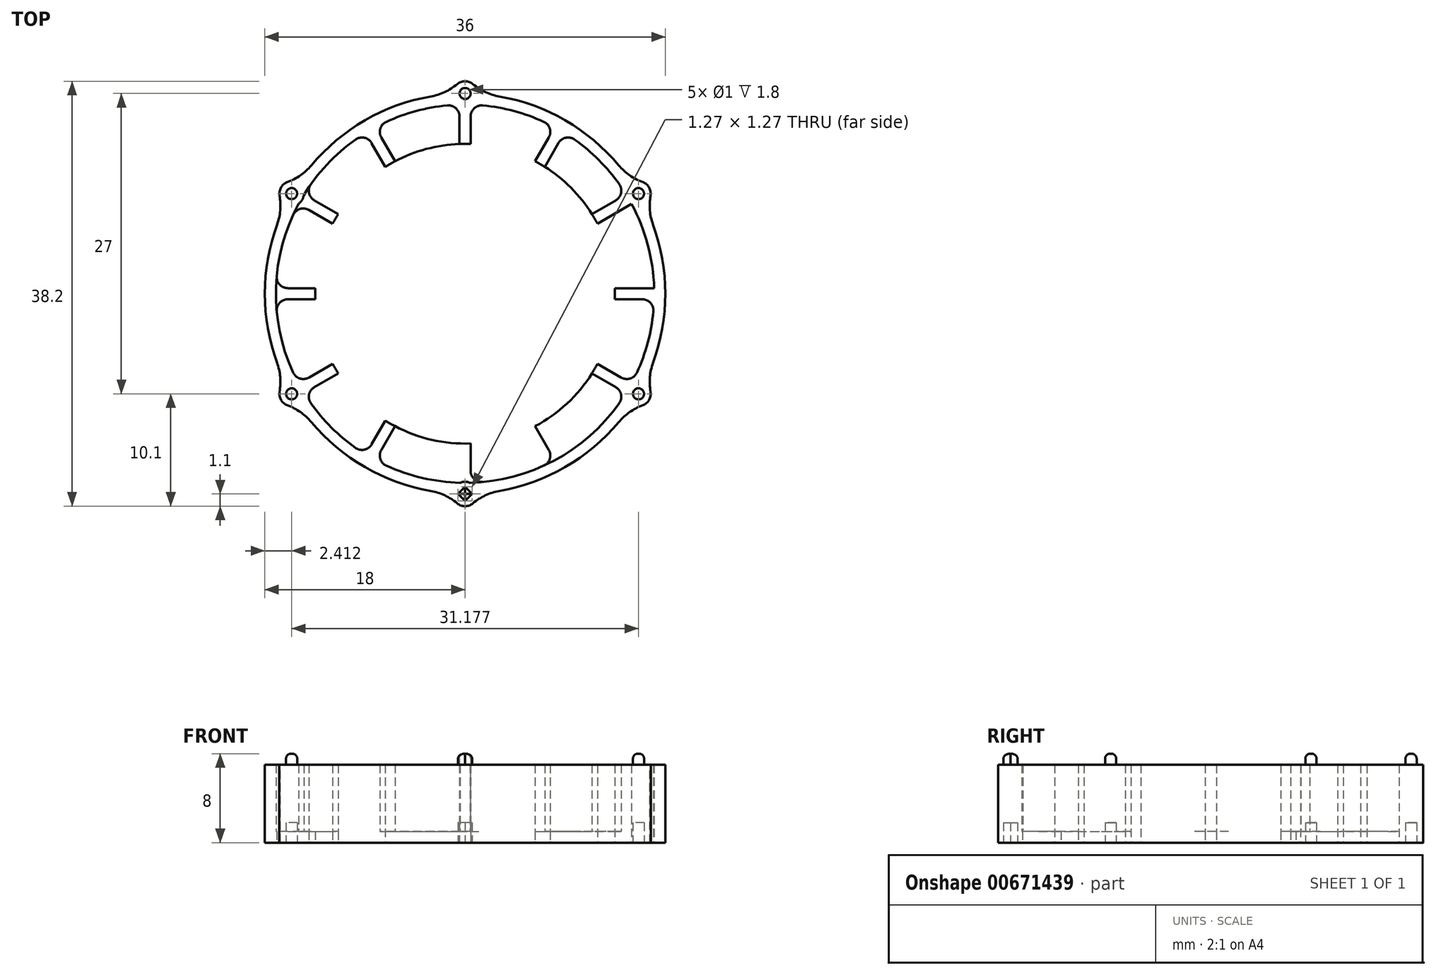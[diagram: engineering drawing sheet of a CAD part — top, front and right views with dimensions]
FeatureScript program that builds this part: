
annotation { "Feature Type Name" : "Feature", "Feature Type Description" : "" }
export const myFeature = defineFeature(function(context is Context, id is Id, definition is map)
    precondition{}
    {
        {
            var Q0;
            Q0=qCreatedBy(makeId("Top.planeOp"),FACE);
            var sketch = newSketch(context, id + "F0", { "sketchPlane" : qUnion([Q0])});
            skCircle(sketch, "E0", {"center": v(0, 0) * mm, "radius": 18 * mm});
            skCircle(sketch, "E1.0", {"center": v(0, 0) * mm, "radius": 17 * mm});
            skLineSegment(sketch, "E2.bottom", {"start": v(8.56, 15.83) * mm, "end": v(9.43, 15.33) * mm});
            skLineSegment(sketch, "E2.top", {"start": v(-9.43, -15.33) * mm, "end": v(-8.56, -15.83) * mm});
            skLineSegment(sketch, "E2.left", {"start": v(8.56, 15.83) * mm, "end": v(-9.43, -15.33) * mm});
            skLineSegment(sketch, "E2.right", {"start": v(9.43, 15.33) * mm, "end": v(-8.56, -15.83) * mm});
            skLineSegment(sketch, "E3.bottom", {"start": v(15.33, 9.43) * mm, "end": v(15.83, 8.56) * mm});
            skLineSegment(sketch, "E3.top", {"start": v(-15.83, -8.56) * mm, "end": v(-15.33, -9.43) * mm});
            skLineSegment(sketch, "E3.left", {"start": v(15.33, 9.43) * mm, "end": v(-15.83, -8.56) * mm});
            skLineSegment(sketch, "E3.right", {"start": v(15.83, 8.56) * mm, "end": v(-15.33, -9.43) * mm});
            skLineSegment(sketch, "E4", {"start": v(-38.35, 0) * mm, "end": v(39.17, 0) * mm, "construction": true});
            skLineSegment(sketch, "E5", {"start": v(0, 42.5) * mm, "end": v(0, -42.47) * mm, "construction": true});
            skLineSegment(sketch, "E6.bottom", {"start": v(-18, 0.5) * mm, "end": v(18, 0.5) * mm});
            skLineSegment(sketch, "E6.top", {"start": v(-18, -0.5) * mm, "end": v(18, -0.5) * mm});
            skLineSegment(sketch, "E6.left", {"start": v(-18, 0.5) * mm, "end": v(-18, -0.5) * mm});
            skLineSegment(sketch, "E6.right", {"start": v(18, 0.5) * mm, "end": v(18, -0.5) * mm});
            skLineSegment(sketch, "E7.bottom", {"start": v(-15.33, 9.43) * mm, "end": v(15.83, -8.56) * mm});
            skLineSegment(sketch, "E7.top", {"start": v(-15.83, 8.56) * mm, "end": v(15.33, -9.43) * mm});
            skLineSegment(sketch, "E7.left", {"start": v(-15.33, 9.43) * mm, "end": v(-15.83, 8.56) * mm});
            skLineSegment(sketch, "E7.right", {"start": v(15.83, -8.56) * mm, "end": v(15.33, -9.43) * mm});
            skLineSegment(sketch, "E8.bottom", {"start": v(-0.5, 18) * mm, "end": v(0.5, 18) * mm});
            skLineSegment(sketch, "E8.top", {"start": v(-0.5, -18) * mm, "end": v(0.5, -18) * mm});
            skLineSegment(sketch, "E8.left", {"start": v(-0.5, 18) * mm, "end": v(-0.5, -18) * mm});
            skLineSegment(sketch, "E8.right", {"start": v(0.5, 18) * mm, "end": v(0.5, -18) * mm});
            skLineSegment(sketch, "E9.bottom", {"start": v(-9.43, 15.33) * mm, "end": v(-8.56, 15.83) * mm});
            skLineSegment(sketch, "E9.top", {"start": v(8.56, -15.83) * mm, "end": v(9.43, -15.33) * mm});
            skLineSegment(sketch, "E9.left", {"start": v(-9.43, 15.33) * mm, "end": v(8.56, -15.83) * mm});
            skLineSegment(sketch, "E9.right", {"start": v(-8.56, 15.83) * mm, "end": v(9.43, -15.33) * mm});
            skCircle(sketch, "E10", {"center": v(0, 0) * mm, "radius": 13.47 * mm});
            skSolve(sketch);
        }
        {
            var Q0;
            Q0=qCreatedBy(makeId("Top.planeOp"),FACE);
            var sketch = newSketch(context, id + "F1", { "sketchPlane" : qUnion([Q0])});
            skCircle(sketch, "E11", {"center": v(0, 0) * mm, "radius": 18 * mm});
            skCircle(sketch, "E12", {"center": v(0, 0) * mm, "radius": 17 * mm});
            skSolve(sketch);
        }
        {
            var Q0;
            Q0=makeQuery(id+"F1.imprint","IMPRINT",FACE,{"disambiguationData":[TD([[makeQuery(id+"F1.imprint","IMPRINT",EDGE,{"derivedFrom":sQuery(id+"F1.wireOp",EDGE,"E11")}),1.0]])]});
            extrude(context, id + "F2", {"entities" : qUnion([Q0]), "depth" : 7 * mm, "offsetDistance" : 25 * mm});
        }
        {
            var Q0;
            {var subQ0=sQuery(id+"F0.wireOp",EDGE,"E2.right");var subQ1=sQuery(id+"F0.wireOp",EDGE,"E1.0");var subQ2=makeQuery(id+"F0.imprint","INTERSECT",VERTEX,{"disambiguationData":[OD(0.0)],"derivedFrom":[subQ1,subQ0]});Q0=makeQuery(id+"F0.imprint","IMPRINT",FACE,{"disambiguationData":[TD([[makeQuery(id+"F0.imprint","IMPRINT",EDGE,{"disambiguationData":[TD([[subQ2,-1.0]])],"derivedFrom":subQ1}),1.0]])]});}
            var Q1;
            {var subQ0=sQuery(id+"F0.wireOp",EDGE,"E6.bottom");var subQ1=sQuery(id+"F0.wireOp",EDGE,"E1.0");var subQ2=makeQuery(id+"F0.imprint","INTERSECT",VERTEX,{"disambiguationData":[OD(0.0)],"derivedFrom":[subQ1,subQ0]});Q1=makeQuery(id+"F0.imprint","IMPRINT",FACE,{"disambiguationData":[TD([[makeQuery(id+"F0.imprint","IMPRINT",EDGE,{"disambiguationData":[TD([[subQ2,1.0]])],"derivedFrom":subQ1}),1.0]])]});}
            var Q2;
            {var subQ0=sQuery(id+"F0.wireOp",EDGE,"E3.left");var subQ1=sQuery(id+"F0.wireOp",EDGE,"E1.0");var subQ2=makeQuery(id+"F0.imprint","INTERSECT",VERTEX,{"disambiguationData":[OD(1.0)],"derivedFrom":[subQ1,subQ0]});Q2=makeQuery(id+"F0.imprint","IMPRINT",FACE,{"disambiguationData":[TD([[makeQuery(id+"F0.imprint","IMPRINT",EDGE,{"disambiguationData":[TD([[subQ2,-1.0]])],"derivedFrom":subQ1}),1.0]])]});}
            var Q3;
            {var subQ0=sQuery(id+"F0.wireOp",EDGE,"E9.right");var subQ1=sQuery(id+"F0.wireOp",EDGE,"E1.0");var subQ2=makeQuery(id+"F0.imprint","INTERSECT",VERTEX,{"disambiguationData":[OD(0.0)],"derivedFrom":[subQ1,subQ0]});Q3=makeQuery(id+"F0.imprint","IMPRINT",FACE,{"disambiguationData":[TD([[makeQuery(id+"F0.imprint","IMPRINT",EDGE,{"disambiguationData":[TD([[subQ2,-1.0]])],"derivedFrom":subQ1}),1.0]])]});}
            var Q4;
            {var subQ0=sQuery(id+"F0.wireOp",EDGE,"E8.right");var subQ1=sQuery(id+"F0.wireOp",EDGE,"E1.0");var subQ2=makeQuery(id+"F0.imprint","INTERSECT",VERTEX,{"disambiguationData":[OD(0.0)],"derivedFrom":[subQ1,subQ0]});Q4=makeQuery(id+"F0.imprint","IMPRINT",FACE,{"disambiguationData":[TD([[makeQuery(id+"F0.imprint","IMPRINT",EDGE,{"disambiguationData":[TD([[subQ2,-1.0]])],"derivedFrom":subQ1}),1.0]])]});}
            var Q5;
            {var subQ0=sQuery(id+"F0.wireOp",EDGE,"E3.right");var subQ1=sQuery(id+"F0.wireOp",EDGE,"E1.0");var subQ2=makeQuery(id+"F0.imprint","INTERSECT",VERTEX,{"disambiguationData":[OD(0.0)],"derivedFrom":[subQ1,subQ0]});Q5=makeQuery(id+"F0.imprint","IMPRINT",FACE,{"disambiguationData":[TD([[makeQuery(id+"F0.imprint","IMPRINT",EDGE,{"disambiguationData":[TD([[subQ2,-1.0]])],"derivedFrom":subQ1}),1.0]])]});}
            var Q6;
            {var subQ0=sQuery(id+"F0.wireOp",EDGE,"E7.top");var subQ1=sQuery(id+"F0.wireOp",EDGE,"E1.0");var subQ2=makeQuery(id+"F0.imprint","INTERSECT",VERTEX,{"disambiguationData":[OD(1.0)],"derivedFrom":[subQ1,subQ0]});Q6=makeQuery(id+"F0.imprint","IMPRINT",FACE,{"disambiguationData":[TD([[makeQuery(id+"F0.imprint","IMPRINT",EDGE,{"disambiguationData":[TD([[subQ2,-1.0]])],"derivedFrom":subQ1}),1.0]])]});}
            var Q7;
            {var subQ0=sQuery(id+"F0.wireOp",EDGE,"E2.left");var subQ1=sQuery(id+"F0.wireOp",EDGE,"E1.0");var subQ2=makeQuery(id+"F0.imprint","INTERSECT",VERTEX,{"disambiguationData":[OD(1.0)],"derivedFrom":[subQ1,subQ0]});Q7=makeQuery(id+"F0.imprint","IMPRINT",FACE,{"disambiguationData":[TD([[makeQuery(id+"F0.imprint","IMPRINT",EDGE,{"disambiguationData":[TD([[subQ2,-1.0]])],"derivedFrom":subQ1}),1.0]])]});}
            extrude(context, id + "F3", {"entities" : qUnion([Q0, Q1, Q2, Q3, Q4, Q5, Q6, Q7]), "operationType" : NewBodyOperationType.ADD, "depth" : 7 * mm, "offsetDistance" : 25 * mm});
        }
        {
            var Q0;
            Q0=makeQuery(id+"F1.imprint","IMPRINT",FACE,{"disambiguationData":[TD([[makeQuery(id+"F1.imprint","IMPRINT",EDGE,{"derivedFrom":sQuery(id+"F1.wireOp",EDGE,"E11")}),1.0]])]});
            var Q1;
            Q1=makeQuery(id+"F1.imprint","IMPRINT",FACE,{"disambiguationData":[TD([[makeQuery(id+"F1.imprint","IMPRINT",EDGE,{"derivedFrom":sQuery(id+"F1.wireOp",EDGE,"E12")}),1.0]])]});
            extrude(context, id + "F4", {"entities" : qUnion([Q0, Q1]), "operationType" : NewBodyOperationType.ADD, "depth" : 1 * mm, "offsetDistance" : 25 * mm});
        }
        {
            var Q0;
            Q0=qCreatedBy(makeId("Top.planeOp"),FACE);
            var sketch = newSketch(context, id + "F5", { "sketchPlane" : qUnion([Q0])});
            skCircle(sketch, "E13", {"center": v(0, 0) * mm, "radius": 18 * mm});
            skLineSegment(sketch, "E14", {"start": v(0, 18) * mm, "end": v(0, -18) * mm, "construction": true});
            skLineSegment(sketch, "E15", {"start": v(15.59, 9) * mm, "end": v(0, 0) * mm, "construction": true});
            skLineSegment(sketch, "E16", {"start": v(9, 15.59) * mm, "end": v(0, 0) * mm, "construction": true});
            skLineSegment(sketch, "E17", {"start": v(0, 0) * mm, "end": v(18, 0) * mm, "construction": true});
            skLineSegment(sketch, "E18", {"start": v(0, 0) * mm, "end": v(15.59, -9) * mm, "construction": true});
            skLineSegment(sketch, "E19", {"start": v(0, 0) * mm, "end": v(9, -15.59) * mm, "construction": true});
            skLineSegment(sketch, "E20", {"start": v(0, 0) * mm, "end": v(-9, 15.59) * mm, "construction": true});
            skLineSegment(sketch, "E21", {"start": v(0, 0) * mm, "end": v(-15.59, 9) * mm, "construction": true});
            skLineSegment(sketch, "E22", {"start": v(0, 0) * mm, "end": v(-18, 0) * mm, "construction": true});
            skLineSegment(sketch, "E23", {"start": v(0, 0) * mm, "end": v(-15.59, -9) * mm, "construction": true});
            skLineSegment(sketch, "E24", {"start": v(0, 0) * mm, "end": v(-9, -15.59) * mm, "construction": true});
            skCircle(sketch, "E25", {"center": v(0, 18) * mm, "radius": 1.1 * mm});
            skCircle(sketch, "E26", {"center": v(15.59, 9) * mm, "radius": 1.1 * mm});
            skCircle(sketch, "E27", {"center": v(15.59, -9) * mm, "radius": 1.1 * mm});
            skCircle(sketch, "E28", {"center": v(0, -18) * mm, "radius": 1.1 * mm});
            skCircle(sketch, "E29", {"center": v(-15.59, -9) * mm, "radius": 1.1 * mm});
            skCircle(sketch, "E30", {"center": v(-15.59, 9) * mm, "radius": 1.1 * mm});
            skCircle(sketch, "E31", {"center": v(-15.59, 9) * mm, "radius": 0.5 * mm});
            skCircle(sketch, "E32", {"center": v(0, 18) * mm, "radius": 0.5 * mm});
            skCircle(sketch, "E33", {"center": v(15.59, 9) * mm, "radius": 0.5 * mm});
            skCircle(sketch, "E34", {"center": v(15.59, -9) * mm, "radius": 0.5 * mm});
            skCircle(sketch, "E35", {"center": v(-15.59, -9) * mm, "radius": 0.5 * mm});
            skLineSegment(sketch, "E36.bottom", {"start": v(0.64, -18) * mm, "end": v(0, -18.64) * mm});
            skLineSegment(sketch, "E36.top", {"start": v(0, -17.36) * mm, "end": v(-0.64, -18) * mm});
            skLineSegment(sketch, "E36.left", {"start": v(0.64, -18) * mm, "end": v(0, -17.36) * mm});
            skLineSegment(sketch, "E36.right", {"start": v(0, -18.64) * mm, "end": v(-0.64, -18) * mm});
            skSolve(sketch);
        }
        {
            var Q0;
            {var subQ0=sQuery(id+"F5.wireOp",EDGE,"E30");var subQ1=sQuery(id+"F5.wireOp",EDGE,"E13");var subQ2=makeQuery(id+"F5.imprint","INTERSECT",VERTEX,{"disambiguationData":[OD(0.0)],"derivedFrom":[subQ1,subQ0]});Q0=makeQuery(id+"F5.imprint","IMPRINT",FACE,{"disambiguationData":[TD([[makeQuery(id+"F5.imprint","IMPRINT",EDGE,{"disambiguationData":[TD([[subQ2,-1.0]])],"derivedFrom":subQ1}),1.0]])]});}
            var Q1;
            {var subQ0=sQuery(id+"F5.wireOp",EDGE,"E30");var subQ1=sQuery(id+"F5.wireOp",EDGE,"E13");var subQ2=makeQuery(id+"F5.imprint","INTERSECT",VERTEX,{"disambiguationData":[OD(0.0)],"derivedFrom":[subQ1,subQ0]});Q1=makeQuery(id+"F5.imprint","IMPRINT",FACE,{"disambiguationData":[TD([[makeQuery(id+"F5.imprint","IMPRINT",EDGE,{"disambiguationData":[TD([[subQ2,-1.0]])],"derivedFrom":subQ1}),-1.0]])]});}
            var Q2;
            {var subQ0=sQuery(id+"F5.wireOp",EDGE,"E25");var subQ1=sQuery(id+"F5.wireOp",EDGE,"E13");var subQ2=makeQuery(id+"F5.imprint","INTERSECT",VERTEX,{"disambiguationData":[OD(0.0)],"derivedFrom":[subQ1,subQ0]});Q2=makeQuery(id+"F5.imprint","IMPRINT",FACE,{"disambiguationData":[TD([[makeQuery(id+"F5.imprint","IMPRINT",EDGE,{"disambiguationData":[TD([[subQ2,-1.0]])],"derivedFrom":subQ1}),1.0]])]});}
            var Q3;
            {var subQ0=sQuery(id+"F5.wireOp",EDGE,"E25");var subQ1=sQuery(id+"F5.wireOp",EDGE,"E13");var subQ2=makeQuery(id+"F5.imprint","INTERSECT",VERTEX,{"disambiguationData":[OD(0.0)],"derivedFrom":[subQ1,subQ0]});Q3=makeQuery(id+"F5.imprint","IMPRINT",FACE,{"disambiguationData":[TD([[makeQuery(id+"F5.imprint","IMPRINT",EDGE,{"disambiguationData":[TD([[subQ2,-1.0]])],"derivedFrom":subQ1}),-1.0]])]});}
            var Q4;
            {var subQ0=sQuery(id+"F5.wireOp",EDGE,"E26");var subQ1=sQuery(id+"F5.wireOp",EDGE,"E13");var subQ2=makeQuery(id+"F5.imprint","INTERSECT",VERTEX,{"disambiguationData":[OD(0.0)],"derivedFrom":[subQ1,subQ0]});Q4=makeQuery(id+"F5.imprint","IMPRINT",FACE,{"disambiguationData":[TD([[makeQuery(id+"F5.imprint","IMPRINT",EDGE,{"disambiguationData":[TD([[subQ2,-1.0]])],"derivedFrom":subQ1}),-1.0]])]});}
            var Q5;
            {var subQ0=sQuery(id+"F5.wireOp",EDGE,"E26");var subQ1=sQuery(id+"F5.wireOp",EDGE,"E13");var subQ2=makeQuery(id+"F5.imprint","INTERSECT",VERTEX,{"disambiguationData":[OD(0.0)],"derivedFrom":[subQ1,subQ0]});Q5=makeQuery(id+"F5.imprint","IMPRINT",FACE,{"disambiguationData":[TD([[makeQuery(id+"F5.imprint","IMPRINT",EDGE,{"disambiguationData":[TD([[subQ2,-1.0]])],"derivedFrom":subQ1}),1.0]])]});}
            var Q6;
            {var subQ0=sQuery(id+"F5.wireOp",EDGE,"E29");var subQ1=sQuery(id+"F5.wireOp",EDGE,"E13");var subQ2=makeQuery(id+"F5.imprint","INTERSECT",VERTEX,{"disambiguationData":[OD(0.0)],"derivedFrom":[subQ1,subQ0]});Q6=makeQuery(id+"F5.imprint","IMPRINT",FACE,{"disambiguationData":[TD([[makeQuery(id+"F5.imprint","IMPRINT",EDGE,{"disambiguationData":[TD([[subQ2,-1.0]])],"derivedFrom":subQ1}),1.0]])]});}
            var Q7;
            {var subQ0=sQuery(id+"F5.wireOp",EDGE,"E29");var subQ1=sQuery(id+"F5.wireOp",EDGE,"E13");var subQ2=makeQuery(id+"F5.imprint","INTERSECT",VERTEX,{"disambiguationData":[OD(0.0)],"derivedFrom":[subQ1,subQ0]});Q7=makeQuery(id+"F5.imprint","IMPRINT",FACE,{"disambiguationData":[TD([[makeQuery(id+"F5.imprint","IMPRINT",EDGE,{"disambiguationData":[TD([[subQ2,-1.0]])],"derivedFrom":subQ1}),-1.0]])]});}
            var Q8;
            {var subQ3=sQuery(id+"F5.wireOp",EDGE,"E13");var subQ5=sQuery(id+"F5.wireOp",EDGE,"E28");var subQ6=makeQuery(id+"F5.imprint","INTERSECT",VERTEX,{"disambiguationData":[OD(0.0)],"derivedFrom":[subQ3,subQ5]});Q8=makeQuery(id+"F5.imprint","IMPRINT",FACE,{"disambiguationData":[TD([[makeQuery(id+"F5.imprint","IMPRINT",EDGE,{"disambiguationData":[TD([[subQ6,-1.0]])],"derivedFrom":subQ3}),1.0]])]});}
            var Q9;
            {var subQ6=sQuery(id+"F5.wireOp",EDGE,"E36.bottom");Q9=makeQuery(id+"F5.imprint","IMPRINT",FACE,{"disambiguationData":[TD([[makeQuery(id+"F5.imprint","IMPRINT",EDGE,{"derivedFrom":subQ6}),1.0]])]});}
            var Q10;
            {var subQ0=sQuery(id+"F5.wireOp",EDGE,"E27");var subQ1=sQuery(id+"F5.wireOp",EDGE,"E13");var subQ2=makeQuery(id+"F5.imprint","INTERSECT",VERTEX,{"disambiguationData":[OD(0.0)],"derivedFrom":[subQ1,subQ0]});Q10=makeQuery(id+"F5.imprint","IMPRINT",FACE,{"disambiguationData":[TD([[makeQuery(id+"F5.imprint","IMPRINT",EDGE,{"disambiguationData":[TD([[subQ2,-1.0]])],"derivedFrom":subQ1}),-1.0]])]});}
            var Q11;
            {var subQ0=sQuery(id+"F5.wireOp",EDGE,"E27");var subQ1=sQuery(id+"F5.wireOp",EDGE,"E13");var subQ2=makeQuery(id+"F5.imprint","INTERSECT",VERTEX,{"disambiguationData":[OD(0.0)],"derivedFrom":[subQ1,subQ0]});Q11=makeQuery(id+"F5.imprint","IMPRINT",FACE,{"disambiguationData":[TD([[makeQuery(id+"F5.imprint","IMPRINT",EDGE,{"disambiguationData":[TD([[subQ2,-1.0]])],"derivedFrom":subQ1}),1.0]])]});}
            var Q12;
            {var subQ0=sQuery(id+"F5.wireOp",EDGE,"E31");var subQ1=sQuery(id+"F5.wireOp",EDGE,"E13");var subQ2=makeQuery(id+"F5.imprint","INTERSECT",VERTEX,{"disambiguationData":[OD(0.0)],"derivedFrom":[subQ1,subQ0]});Q12=makeQuery(id+"F5.imprint","IMPRINT",FACE,{"disambiguationData":[TD([[makeQuery(id+"F5.imprint","IMPRINT",EDGE,{"disambiguationData":[TD([[subQ2,-1.0]])],"derivedFrom":subQ1}),1.0]])]});}
            var Q13;
            {var subQ0=sQuery(id+"F5.wireOp",EDGE,"E31");var subQ1=sQuery(id+"F5.wireOp",EDGE,"E13");var subQ2=makeQuery(id+"F5.imprint","INTERSECT",VERTEX,{"disambiguationData":[OD(0.0)],"derivedFrom":[subQ1,subQ0]});Q13=makeQuery(id+"F5.imprint","IMPRINT",FACE,{"disambiguationData":[TD([[makeQuery(id+"F5.imprint","IMPRINT",EDGE,{"disambiguationData":[TD([[subQ2,-1.0]])],"derivedFrom":subQ1}),-1.0]])]});}
            var Q14;
            {var subQ0=sQuery(id+"F5.wireOp",EDGE,"E32");var subQ1=sQuery(id+"F5.wireOp",EDGE,"E13");var subQ2=makeQuery(id+"F5.imprint","INTERSECT",VERTEX,{"disambiguationData":[OD(0.0)],"derivedFrom":[subQ1,subQ0]});Q14=makeQuery(id+"F5.imprint","IMPRINT",FACE,{"disambiguationData":[TD([[makeQuery(id+"F5.imprint","IMPRINT",EDGE,{"disambiguationData":[TD([[subQ2,-1.0]])],"derivedFrom":subQ1}),-1.0]])]});}
            var Q15;
            {var subQ0=sQuery(id+"F5.wireOp",EDGE,"E32");var subQ1=sQuery(id+"F5.wireOp",EDGE,"E13");var subQ2=makeQuery(id+"F5.imprint","INTERSECT",VERTEX,{"disambiguationData":[OD(0.0)],"derivedFrom":[subQ1,subQ0]});Q15=makeQuery(id+"F5.imprint","IMPRINT",FACE,{"disambiguationData":[TD([[makeQuery(id+"F5.imprint","IMPRINT",EDGE,{"disambiguationData":[TD([[subQ2,-1.0]])],"derivedFrom":subQ1}),1.0]])]});}
            var Q16;
            {var subQ0=sQuery(id+"F5.wireOp",EDGE,"E33");var subQ1=sQuery(id+"F5.wireOp",EDGE,"E13");var subQ2=makeQuery(id+"F5.imprint","INTERSECT",VERTEX,{"disambiguationData":[OD(0.0)],"derivedFrom":[subQ1,subQ0]});Q16=makeQuery(id+"F5.imprint","IMPRINT",FACE,{"disambiguationData":[TD([[makeQuery(id+"F5.imprint","IMPRINT",EDGE,{"disambiguationData":[TD([[subQ2,-1.0]])],"derivedFrom":subQ1}),-1.0]])]});}
            var Q17;
            {var subQ0=sQuery(id+"F5.wireOp",EDGE,"E33");var subQ1=sQuery(id+"F5.wireOp",EDGE,"E13");var subQ2=makeQuery(id+"F5.imprint","INTERSECT",VERTEX,{"disambiguationData":[OD(0.0)],"derivedFrom":[subQ1,subQ0]});Q17=makeQuery(id+"F5.imprint","IMPRINT",FACE,{"disambiguationData":[TD([[makeQuery(id+"F5.imprint","IMPRINT",EDGE,{"disambiguationData":[TD([[subQ2,-1.0]])],"derivedFrom":subQ1}),1.0]])]});}
            var Q18;
            {var subQ0=sQuery(id+"F5.wireOp",EDGE,"E34");var subQ1=sQuery(id+"F5.wireOp",EDGE,"E13");var subQ2=makeQuery(id+"F5.imprint","INTERSECT",VERTEX,{"disambiguationData":[OD(0.0)],"derivedFrom":[subQ1,subQ0]});Q18=makeQuery(id+"F5.imprint","IMPRINT",FACE,{"disambiguationData":[TD([[makeQuery(id+"F5.imprint","IMPRINT",EDGE,{"disambiguationData":[TD([[subQ2,-1.0]])],"derivedFrom":subQ1}),-1.0]])]});}
            var Q19;
            {var subQ0=sQuery(id+"F5.wireOp",EDGE,"E34");var subQ1=sQuery(id+"F5.wireOp",EDGE,"E13");var subQ2=makeQuery(id+"F5.imprint","INTERSECT",VERTEX,{"disambiguationData":[OD(0.0)],"derivedFrom":[subQ1,subQ0]});Q19=makeQuery(id+"F5.imprint","IMPRINT",FACE,{"disambiguationData":[TD([[makeQuery(id+"F5.imprint","IMPRINT",EDGE,{"disambiguationData":[TD([[subQ2,-1.0]])],"derivedFrom":subQ1}),1.0]])]});}
            var Q20;
            {var subQ1=sQuery(id+"F5.wireOp",EDGE,"E36.bottom");Q20=makeQuery(id+"F5.imprint","IMPRINT",FACE,{"disambiguationData":[TD([[makeQuery(id+"F5.imprint","IMPRINT",EDGE,{"derivedFrom":subQ1}),-1.0]])]});}
            var Q21;
            {var subQ0=sQuery(id+"F5.wireOp",EDGE,"E35");var subQ1=sQuery(id+"F5.wireOp",EDGE,"E13");var subQ2=makeQuery(id+"F5.imprint","INTERSECT",VERTEX,{"disambiguationData":[OD(0.0)],"derivedFrom":[subQ1,subQ0]});Q21=makeQuery(id+"F5.imprint","IMPRINT",FACE,{"disambiguationData":[TD([[makeQuery(id+"F5.imprint","IMPRINT",EDGE,{"disambiguationData":[TD([[subQ2,-1.0]])],"derivedFrom":subQ1}),-1.0]])]});}
            var Q22;
            {var subQ0=sQuery(id+"F5.wireOp",EDGE,"E35");var subQ1=sQuery(id+"F5.wireOp",EDGE,"E13");var subQ2=makeQuery(id+"F5.imprint","INTERSECT",VERTEX,{"disambiguationData":[OD(0.0)],"derivedFrom":[subQ1,subQ0]});Q22=makeQuery(id+"F5.imprint","IMPRINT",FACE,{"disambiguationData":[TD([[makeQuery(id+"F5.imprint","IMPRINT",EDGE,{"disambiguationData":[TD([[subQ2,-1.0]])],"derivedFrom":subQ1}),1.0]])]});}
            var Q23;
            {var subQ0=sQuery(id+"F5.wireOp",EDGE,"E36.top");var subQ1=sQuery(id+"F5.wireOp",EDGE,"E13");var subQ2=makeQuery(id+"F5.imprint","INTERSECT",VERTEX,{"derivedFrom":[subQ1,subQ0]});Q23=makeQuery(id+"F5.imprint","IMPRINT",FACE,{"disambiguationData":[TD([[makeQuery(id+"F5.imprint","IMPRINT",EDGE,{"disambiguationData":[TD([[subQ2,-1.0]])],"derivedFrom":subQ1}),1.0]])]});}
            extrude(context, id + "F6", {"entities" : qUnion([Q0, Q1, Q2, Q3, Q4, Q5, Q6, Q7, Q8, Q9, Q10, Q11, Q12, Q13, Q14, Q15, Q16, Q17, Q18, Q19, Q20, Q21, Q22, Q23]), "operationType" : NewBodyOperationType.ADD, "depth" : 7 * mm, "offsetDistance" : 25 * mm});
        }
        {
            var Q0;
            {var subQ0=sQuery(id+"F0.wireOp",EDGE,"E8.right");var subQ1=sQuery(id+"F0.wireOp",EDGE,"E1.0");Q0=makeQuery(id+"F3.opExtrude","SWEPT_EDGE",EDGE,{"disambiguationData":[OSD([subQ1,subQ0]),TDD([makeQuery(id+"F0.imprint","INTERSECT",VERTEX,{"disambiguationData":[OD(1.0)],"derivedFrom":[subQ1,subQ0]})])]});}
            var Q1;
            {var subQ0=sQuery(id+"F0.wireOp",EDGE,"E2.left");var subQ1=sQuery(id+"F0.wireOp",EDGE,"E1.0");Q1=makeQuery(id+"F3.opExtrude","SWEPT_EDGE",EDGE,{"disambiguationData":[OSD([subQ1,subQ0]),TDD([makeQuery(id+"F0.imprint","INTERSECT",VERTEX,{"disambiguationData":[OD(1.0)],"derivedFrom":[subQ1,subQ0]})])]});}
            var Q2;
            {var subQ0=sQuery(id+"F0.wireOp",EDGE,"E3.left");var subQ1=sQuery(id+"F0.wireOp",EDGE,"E1.0");Q2=makeQuery(id+"F3.opExtrude","SWEPT_EDGE",EDGE,{"disambiguationData":[OSD([subQ1,subQ0]),TDD([makeQuery(id+"F0.imprint","INTERSECT",VERTEX,{"disambiguationData":[OD(1.0)],"derivedFrom":[subQ1,subQ0]})])]});}
            var Q3;
            {var subQ0=sQuery(id+"F0.wireOp",EDGE,"E6.bottom");var subQ1=sQuery(id+"F0.wireOp",EDGE,"E1.0");Q3=makeQuery(id+"F3.opExtrude","SWEPT_EDGE",EDGE,{"disambiguationData":[OSD([subQ1,subQ0]),TDD([makeQuery(id+"F0.imprint","INTERSECT",VERTEX,{"disambiguationData":[OD(1.0)],"derivedFrom":[subQ1,subQ0]})])]});}
            var Q4;
            {var subQ0=sQuery(id+"F0.wireOp",EDGE,"E9.right");var subQ1=sQuery(id+"F0.wireOp",EDGE,"E1.0");Q4=makeQuery(id+"F3.opExtrude","SWEPT_EDGE",EDGE,{"disambiguationData":[OSD([subQ1,subQ0]),TDD([makeQuery(id+"F0.imprint","INTERSECT",VERTEX,{"disambiguationData":[OD(1.0)],"derivedFrom":[subQ1,subQ0]})])]});}
            var Q5;
            {var subQ0=sQuery(id+"F0.wireOp",EDGE,"E7.bottom");var subQ1=sQuery(id+"F0.wireOp",EDGE,"E1.0");Q5=makeQuery(id+"F3.opExtrude","SWEPT_EDGE",EDGE,{"disambiguationData":[OSD([subQ1,subQ0]),TDD([makeQuery(id+"F0.imprint","INTERSECT",VERTEX,{"disambiguationData":[OD(1.0)],"derivedFrom":[subQ1,subQ0]})])]});}
            var Q6;
            {var subQ0=sQuery(id+"F0.wireOp",EDGE,"E8.left");var subQ1=sQuery(id+"F0.wireOp",EDGE,"E1.0");Q6=makeQuery(id+"F3.opExtrude","SWEPT_EDGE",EDGE,{"disambiguationData":[OSD([subQ1,subQ0]),TDD([makeQuery(id+"F0.imprint","INTERSECT",VERTEX,{"disambiguationData":[OD(0.0)],"derivedFrom":[subQ1,subQ0]})])]});}
            var Q7;
            {var subQ0=sQuery(id+"F0.wireOp",EDGE,"E2.left");var subQ1=sQuery(id+"F0.wireOp",EDGE,"E1.0");Q7=makeQuery(id+"F3.opExtrude","SWEPT_EDGE",EDGE,{"disambiguationData":[OSD([subQ1,subQ0]),TDD([makeQuery(id+"F0.imprint","INTERSECT",VERTEX,{"disambiguationData":[OD(0.0)],"derivedFrom":[subQ1,subQ0]})])]});}
            var Q8;
            {var subQ0=sQuery(id+"F0.wireOp",EDGE,"E3.left");var subQ1=sQuery(id+"F0.wireOp",EDGE,"E1.0");Q8=makeQuery(id+"F3.opExtrude","SWEPT_EDGE",EDGE,{"disambiguationData":[OSD([subQ1,subQ0]),TDD([makeQuery(id+"F0.imprint","INTERSECT",VERTEX,{"disambiguationData":[OD(0.0)],"derivedFrom":[subQ1,subQ0]})])]});}
            var Q9;
            {var subQ0=sQuery(id+"F0.wireOp",EDGE,"E6.top");var subQ1=sQuery(id+"F0.wireOp",EDGE,"E1.0");Q9=makeQuery(id+"F3.opExtrude","SWEPT_EDGE",EDGE,{"disambiguationData":[OSD([subQ1,subQ0]),TDD([makeQuery(id+"F0.imprint","INTERSECT",VERTEX,{"disambiguationData":[OD(1.0)],"derivedFrom":[subQ1,subQ0]})])]});}
            var Q10;
            {var subQ0=sQuery(id+"F0.wireOp",EDGE,"E7.top");var subQ1=sQuery(id+"F0.wireOp",EDGE,"E1.0");Q10=makeQuery(id+"F3.opExtrude","SWEPT_EDGE",EDGE,{"disambiguationData":[OSD([subQ1,subQ0]),TDD([makeQuery(id+"F0.imprint","INTERSECT",VERTEX,{"disambiguationData":[OD(0.0)],"derivedFrom":[subQ1,subQ0]})])]});}
            var Q11;
            {var subQ0=sQuery(id+"F0.wireOp",EDGE,"E6.top");var subQ1=sQuery(id+"F0.wireOp",EDGE,"E1.0");Q11=makeQuery(id+"F3.opExtrude","SWEPT_EDGE",EDGE,{"disambiguationData":[OSD([subQ1,subQ0]),TDD([makeQuery(id+"F0.imprint","INTERSECT",VERTEX,{"disambiguationData":[OD(0.0)],"derivedFrom":[subQ1,subQ0]})])]});}
            var Q12;
            {var subQ0=sQuery(id+"F0.wireOp",EDGE,"E9.left");var subQ1=sQuery(id+"F0.wireOp",EDGE,"E1.0");Q12=makeQuery(id+"F3.opExtrude","SWEPT_EDGE",EDGE,{"disambiguationData":[OSD([subQ1,subQ0]),TDD([makeQuery(id+"F0.imprint","INTERSECT",VERTEX,{"disambiguationData":[OD(0.0)],"derivedFrom":[subQ1,subQ0]})])]});}
            var Q13;
            {var subQ0=sQuery(id+"F0.wireOp",EDGE,"E8.right");var subQ1=sQuery(id+"F0.wireOp",EDGE,"E1.0");Q13=makeQuery(id+"F3.opExtrude","SWEPT_EDGE",EDGE,{"disambiguationData":[OSD([subQ1,subQ0]),TDD([makeQuery(id+"F0.imprint","INTERSECT",VERTEX,{"disambiguationData":[OD(0.0)],"derivedFrom":[subQ1,subQ0]})])]});}
            var Q14;
            {var subQ0=sQuery(id+"F0.wireOp",EDGE,"E7.bottom");var subQ1=sQuery(id+"F0.wireOp",EDGE,"E1.0");Q14=makeQuery(id+"F3.opExtrude","SWEPT_EDGE",EDGE,{"disambiguationData":[OSD([subQ1,subQ0]),TDD([makeQuery(id+"F0.imprint","INTERSECT",VERTEX,{"disambiguationData":[OD(0.0)],"derivedFrom":[subQ1,subQ0]})])]});}
            var Q15;
            {var subQ0=sQuery(id+"F0.wireOp",EDGE,"E9.right");var subQ1=sQuery(id+"F0.wireOp",EDGE,"E1.0");Q15=makeQuery(id+"F3.opExtrude","SWEPT_EDGE",EDGE,{"disambiguationData":[OSD([subQ1,subQ0]),TDD([makeQuery(id+"F0.imprint","INTERSECT",VERTEX,{"disambiguationData":[OD(0.0)],"derivedFrom":[subQ1,subQ0]})])]});}
            var Q16;
            {var subQ0=sQuery(id+"F0.wireOp",EDGE,"E3.right");var subQ1=sQuery(id+"F0.wireOp",EDGE,"E1.0");Q16=makeQuery(id+"F3.opExtrude","SWEPT_EDGE",EDGE,{"disambiguationData":[OSD([subQ1,subQ0]),TDD([makeQuery(id+"F0.imprint","INTERSECT",VERTEX,{"disambiguationData":[OD(1.0)],"derivedFrom":[subQ1,subQ0]})])]});}
            var Q17;
            {var subQ0=sQuery(id+"F0.wireOp",EDGE,"E2.right");var subQ1=sQuery(id+"F0.wireOp",EDGE,"E1.0");Q17=makeQuery(id+"F3.opExtrude","SWEPT_EDGE",EDGE,{"disambiguationData":[OSD([subQ1,subQ0]),TDD([makeQuery(id+"F0.imprint","INTERSECT",VERTEX,{"disambiguationData":[OD(1.0)],"derivedFrom":[subQ1,subQ0]})])]});}
            var Q18;
            {var subQ0=sQuery(id+"F0.wireOp",EDGE,"E3.right");var subQ1=sQuery(id+"F0.wireOp",EDGE,"E1.0");Q18=makeQuery(id+"F3.opExtrude","SWEPT_EDGE",EDGE,{"disambiguationData":[OSD([subQ1,subQ0]),TDD([makeQuery(id+"F0.imprint","INTERSECT",VERTEX,{"disambiguationData":[OD(0.0)],"derivedFrom":[subQ1,subQ0]})])]});}
            var Q19;
            {var subQ0=sQuery(id+"F0.wireOp",EDGE,"E2.right");var subQ1=sQuery(id+"F0.wireOp",EDGE,"E1.0");Q19=makeQuery(id+"F3.opExtrude","SWEPT_EDGE",EDGE,{"disambiguationData":[OSD([subQ1,subQ0]),TDD([makeQuery(id+"F0.imprint","INTERSECT",VERTEX,{"disambiguationData":[OD(0.0)],"derivedFrom":[subQ1,subQ0]})])]});}
            var Q20;
            {var subQ0=sQuery(id+"F0.wireOp",EDGE,"E8.left");var subQ1=sQuery(id+"F0.wireOp",EDGE,"E1.0");Q20=makeQuery(id+"F3.opExtrude","SWEPT_EDGE",EDGE,{"disambiguationData":[OSD([subQ1,subQ0]),TDD([makeQuery(id+"F0.imprint","INTERSECT",VERTEX,{"disambiguationData":[OD(1.0)],"derivedFrom":[subQ1,subQ0]})])]});}
            var Q21;
            {var subQ0=sQuery(id+"F0.wireOp",EDGE,"E9.left");var subQ1=sQuery(id+"F0.wireOp",EDGE,"E1.0");Q21=makeQuery(id+"F3.opExtrude","SWEPT_EDGE",EDGE,{"disambiguationData":[OSD([subQ1,subQ0]),TDD([makeQuery(id+"F0.imprint","INTERSECT",VERTEX,{"disambiguationData":[OD(1.0)],"derivedFrom":[subQ1,subQ0]})])]});}
            var Q22;
            {var subQ0=sQuery(id+"F0.wireOp",EDGE,"E7.top");var subQ1=sQuery(id+"F0.wireOp",EDGE,"E1.0");Q22=makeQuery(id+"F3.opExtrude","SWEPT_EDGE",EDGE,{"disambiguationData":[OSD([subQ1,subQ0]),TDD([makeQuery(id+"F0.imprint","INTERSECT",VERTEX,{"disambiguationData":[OD(1.0)],"derivedFrom":[subQ1,subQ0]})])]});}
            var Q23;
            {var subQ0=sQuery(id+"F0.wireOp",EDGE,"E6.bottom");var subQ1=sQuery(id+"F0.wireOp",EDGE,"E1.0");Q23=makeQuery(id+"F3.opExtrude","SWEPT_EDGE",EDGE,{"disambiguationData":[OSD([subQ1,subQ0]),TDD([makeQuery(id+"F0.imprint","INTERSECT",VERTEX,{"disambiguationData":[OD(0.0)],"derivedFrom":[subQ1,subQ0]})])]});}
            fillet(context, id + "F7", {"entities" : qUnion([Q0, Q1, Q2, Q3, Q4, Q5, Q6, Q7, Q8, Q9, Q10, Q11, Q12, Q13, Q14, Q15, Q16, Q17, Q18, Q19, Q20, Q21, Q22, Q23]), "radius" : 1 * mm, "tangentPropagation" : true, "allowEdgeOverflow" : false});
        }
        {
            var Q0;
            Q0=makeQuery(id+"F6.boolean.opBoolean","INTERSECT",EDGE,{"disambiguationData":[OD(0.0)],"derivedFrom":[makeQuery(id+"F2.opExtrude","SWEPT_FACE",FACE,{"disambiguationData":[OSD([sQuery(id+"F1.wireOp",EDGE,"E11")])]}),makeQuery(id+"F6.opExtrude","SWEPT_FACE",FACE,{"disambiguationData":[OSD([sQuery(id+"F5.wireOp",EDGE,"E30")])]})]});
            var Q1;
            Q1=makeQuery(id+"F6.boolean.opBoolean","INTERSECT",EDGE,{"disambiguationData":[OD(1.0)],"derivedFrom":[makeQuery(id+"F2.opExtrude","SWEPT_FACE",FACE,{"disambiguationData":[OSD([sQuery(id+"F1.wireOp",EDGE,"E11")])]}),makeQuery(id+"F6.opExtrude","SWEPT_FACE",FACE,{"disambiguationData":[OSD([sQuery(id+"F5.wireOp",EDGE,"E30")])]})]});
            var Q2;
            Q2=makeQuery(id+"F6.boolean.opBoolean","INTERSECT",EDGE,{"disambiguationData":[OD(1.0)],"derivedFrom":[makeQuery(id+"F2.opExtrude","SWEPT_FACE",FACE,{"disambiguationData":[OSD([sQuery(id+"F1.wireOp",EDGE,"E11")])]}),makeQuery(id+"F6.opExtrude","SWEPT_FACE",FACE,{"disambiguationData":[OSD([sQuery(id+"F5.wireOp",EDGE,"E25")])]})]});
            var Q3;
            Q3=makeQuery(id+"F6.boolean.opBoolean","INTERSECT",EDGE,{"disambiguationData":[OD(1.0)],"derivedFrom":[makeQuery(id+"F2.opExtrude","SWEPT_FACE",FACE,{"disambiguationData":[OSD([sQuery(id+"F1.wireOp",EDGE,"E11")])]}),makeQuery(id+"F6.opExtrude","SWEPT_FACE",FACE,{"disambiguationData":[OSD([sQuery(id+"F5.wireOp",EDGE,"E29")])]})]});
            var Q4;
            Q4=makeQuery(id+"F6.boolean.opBoolean","INTERSECT",EDGE,{"disambiguationData":[OD(0.0)],"derivedFrom":[makeQuery(id+"F2.opExtrude","SWEPT_FACE",FACE,{"disambiguationData":[OSD([sQuery(id+"F1.wireOp",EDGE,"E11")])]}),makeQuery(id+"F6.opExtrude","SWEPT_FACE",FACE,{"disambiguationData":[OSD([sQuery(id+"F5.wireOp",EDGE,"E29")])]})]});
            var Q5;
            Q5=makeQuery(id+"F6.boolean.opBoolean","INTERSECT",EDGE,{"disambiguationData":[OD(1.0)],"derivedFrom":[makeQuery(id+"F2.opExtrude","SWEPT_FACE",FACE,{"disambiguationData":[OSD([sQuery(id+"F1.wireOp",EDGE,"E11")])]}),makeQuery(id+"F6.opExtrude","SWEPT_FACE",FACE,{"disambiguationData":[OSD([sQuery(id+"F5.wireOp",EDGE,"E28")])]})]});
            var Q6;
            Q6=makeQuery(id+"F6.boolean.opBoolean","INTERSECT",EDGE,{"disambiguationData":[OD(0.0)],"derivedFrom":[makeQuery(id+"F2.opExtrude","SWEPT_FACE",FACE,{"disambiguationData":[OSD([sQuery(id+"F1.wireOp",EDGE,"E11")])]}),makeQuery(id+"F6.opExtrude","SWEPT_FACE",FACE,{"disambiguationData":[OSD([sQuery(id+"F5.wireOp",EDGE,"E28")])]})]});
            var Q7;
            Q7=makeQuery(id+"F6.boolean.opBoolean","INTERSECT",EDGE,{"disambiguationData":[OD(1.0)],"derivedFrom":[makeQuery(id+"F2.opExtrude","SWEPT_FACE",FACE,{"disambiguationData":[OSD([sQuery(id+"F1.wireOp",EDGE,"E11")])]}),makeQuery(id+"F6.opExtrude","SWEPT_FACE",FACE,{"disambiguationData":[OSD([sQuery(id+"F5.wireOp",EDGE,"E27")])]})]});
            var Q8;
            Q8=makeQuery(id+"F6.boolean.opBoolean","INTERSECT",EDGE,{"disambiguationData":[OD(0.0)],"derivedFrom":[makeQuery(id+"F2.opExtrude","SWEPT_FACE",FACE,{"disambiguationData":[OSD([sQuery(id+"F1.wireOp",EDGE,"E11")])]}),makeQuery(id+"F6.opExtrude","SWEPT_FACE",FACE,{"disambiguationData":[OSD([sQuery(id+"F5.wireOp",EDGE,"E27")])]})]});
            var Q9;
            Q9=makeQuery(id+"F6.boolean.opBoolean","INTERSECT",EDGE,{"disambiguationData":[OD(1.0)],"derivedFrom":[makeQuery(id+"F2.opExtrude","SWEPT_FACE",FACE,{"disambiguationData":[OSD([sQuery(id+"F1.wireOp",EDGE,"E11")])]}),makeQuery(id+"F6.opExtrude","SWEPT_FACE",FACE,{"disambiguationData":[OSD([sQuery(id+"F5.wireOp",EDGE,"E26")])]})]});
            var Q10;
            Q10=makeQuery(id+"F6.boolean.opBoolean","INTERSECT",EDGE,{"disambiguationData":[OD(0.0)],"derivedFrom":[makeQuery(id+"F2.opExtrude","SWEPT_FACE",FACE,{"disambiguationData":[OSD([sQuery(id+"F1.wireOp",EDGE,"E11")])]}),makeQuery(id+"F6.opExtrude","SWEPT_FACE",FACE,{"disambiguationData":[OSD([sQuery(id+"F5.wireOp",EDGE,"E26")])]})]});
            var Q11;
            Q11=makeQuery(id+"F6.boolean.opBoolean","INTERSECT",EDGE,{"disambiguationData":[OD(0.0)],"derivedFrom":[makeQuery(id+"F2.opExtrude","SWEPT_FACE",FACE,{"disambiguationData":[OSD([sQuery(id+"F1.wireOp",EDGE,"E11")])]}),makeQuery(id+"F6.opExtrude","SWEPT_FACE",FACE,{"disambiguationData":[OSD([sQuery(id+"F5.wireOp",EDGE,"E25")])]})]});
            fillet(context, id + "F8", {"entities" : qUnion([Q0, Q1, Q2, Q3, Q4, Q5, Q6, Q7, Q8, Q9, Q10, Q11]), "radius" : 5 * mm, "tangentPropagation" : true, "allowEdgeOverflow" : false});
        }
        {
            var Q0;
            {var subQ0=sQuery(id+"F5.wireOp",EDGE,"E31");var subQ1=sQuery(id+"F5.wireOp",EDGE,"E13");var subQ2=makeQuery(id+"F5.imprint","INTERSECT",VERTEX,{"disambiguationData":[OD(0.0)],"derivedFrom":[subQ1,subQ0]});Q0=makeQuery(id+"F5.imprint","IMPRINT",FACE,{"disambiguationData":[TD([[makeQuery(id+"F5.imprint","IMPRINT",EDGE,{"disambiguationData":[TD([[subQ2,-1.0]])],"derivedFrom":subQ1}),-1.0]])]});}
            var Q1;
            {var subQ0=sQuery(id+"F5.wireOp",EDGE,"E31");var subQ1=sQuery(id+"F5.wireOp",EDGE,"E13");var subQ2=makeQuery(id+"F5.imprint","INTERSECT",VERTEX,{"disambiguationData":[OD(0.0)],"derivedFrom":[subQ1,subQ0]});Q1=makeQuery(id+"F5.imprint","IMPRINT",FACE,{"disambiguationData":[TD([[makeQuery(id+"F5.imprint","IMPRINT",EDGE,{"disambiguationData":[TD([[subQ2,-1.0]])],"derivedFrom":subQ1}),1.0]])]});}
            var Q2;
            {var subQ0=sQuery(id+"F5.wireOp",EDGE,"E32");var subQ1=sQuery(id+"F5.wireOp",EDGE,"E13");var subQ2=makeQuery(id+"F5.imprint","INTERSECT",VERTEX,{"disambiguationData":[OD(0.0)],"derivedFrom":[subQ1,subQ0]});Q2=makeQuery(id+"F5.imprint","IMPRINT",FACE,{"disambiguationData":[TD([[makeQuery(id+"F5.imprint","IMPRINT",EDGE,{"disambiguationData":[TD([[subQ2,-1.0]])],"derivedFrom":subQ1}),-1.0]])]});}
            var Q3;
            {var subQ0=sQuery(id+"F5.wireOp",EDGE,"E32");var subQ1=sQuery(id+"F5.wireOp",EDGE,"E13");var subQ2=makeQuery(id+"F5.imprint","INTERSECT",VERTEX,{"disambiguationData":[OD(0.0)],"derivedFrom":[subQ1,subQ0]});Q3=makeQuery(id+"F5.imprint","IMPRINT",FACE,{"disambiguationData":[TD([[makeQuery(id+"F5.imprint","IMPRINT",EDGE,{"disambiguationData":[TD([[subQ2,-1.0]])],"derivedFrom":subQ1}),1.0]])]});}
            var Q4;
            {var subQ0=sQuery(id+"F5.wireOp",EDGE,"E33");var subQ1=sQuery(id+"F5.wireOp",EDGE,"E13");var subQ2=makeQuery(id+"F5.imprint","INTERSECT",VERTEX,{"disambiguationData":[OD(0.0)],"derivedFrom":[subQ1,subQ0]});Q4=makeQuery(id+"F5.imprint","IMPRINT",FACE,{"disambiguationData":[TD([[makeQuery(id+"F5.imprint","IMPRINT",EDGE,{"disambiguationData":[TD([[subQ2,-1.0]])],"derivedFrom":subQ1}),1.0]])]});}
            var Q5;
            {var subQ0=sQuery(id+"F5.wireOp",EDGE,"E33");var subQ1=sQuery(id+"F5.wireOp",EDGE,"E13");var subQ2=makeQuery(id+"F5.imprint","INTERSECT",VERTEX,{"disambiguationData":[OD(0.0)],"derivedFrom":[subQ1,subQ0]});Q5=makeQuery(id+"F5.imprint","IMPRINT",FACE,{"disambiguationData":[TD([[makeQuery(id+"F5.imprint","IMPRINT",EDGE,{"disambiguationData":[TD([[subQ2,-1.0]])],"derivedFrom":subQ1}),-1.0]])]});}
            var Q6;
            {var subQ0=sQuery(id+"F5.wireOp",EDGE,"E34");var subQ1=sQuery(id+"F5.wireOp",EDGE,"E13");var subQ2=makeQuery(id+"F5.imprint","INTERSECT",VERTEX,{"disambiguationData":[OD(0.0)],"derivedFrom":[subQ1,subQ0]});Q6=makeQuery(id+"F5.imprint","IMPRINT",FACE,{"disambiguationData":[TD([[makeQuery(id+"F5.imprint","IMPRINT",EDGE,{"disambiguationData":[TD([[subQ2,-1.0]])],"derivedFrom":subQ1}),1.0]])]});}
            var Q7;
            {var subQ0=sQuery(id+"F5.wireOp",EDGE,"E34");var subQ1=sQuery(id+"F5.wireOp",EDGE,"E13");var subQ2=makeQuery(id+"F5.imprint","INTERSECT",VERTEX,{"disambiguationData":[OD(0.0)],"derivedFrom":[subQ1,subQ0]});Q7=makeQuery(id+"F5.imprint","IMPRINT",FACE,{"disambiguationData":[TD([[makeQuery(id+"F5.imprint","IMPRINT",EDGE,{"disambiguationData":[TD([[subQ2,-1.0]])],"derivedFrom":subQ1}),-1.0]])]});}
            var Q8;
            {var subQ1=sQuery(id+"F5.wireOp",EDGE,"E36.bottom");Q8=makeQuery(id+"F5.imprint","IMPRINT",FACE,{"disambiguationData":[TD([[makeQuery(id+"F5.imprint","IMPRINT",EDGE,{"derivedFrom":subQ1}),-1.0]])]});}
            var Q9;
            {var subQ0=sQuery(id+"F5.wireOp",EDGE,"E36.top");var subQ1=sQuery(id+"F5.wireOp",EDGE,"E13");var subQ2=makeQuery(id+"F5.imprint","INTERSECT",VERTEX,{"derivedFrom":[subQ1,subQ0]});Q9=makeQuery(id+"F5.imprint","IMPRINT",FACE,{"disambiguationData":[TD([[makeQuery(id+"F5.imprint","IMPRINT",EDGE,{"disambiguationData":[TD([[subQ2,-1.0]])],"derivedFrom":subQ1}),1.0]])]});}
            var Q10;
            {var subQ0=sQuery(id+"F5.wireOp",EDGE,"E35");var subQ1=sQuery(id+"F5.wireOp",EDGE,"E13");var subQ2=makeQuery(id+"F5.imprint","INTERSECT",VERTEX,{"disambiguationData":[OD(0.0)],"derivedFrom":[subQ1,subQ0]});Q10=makeQuery(id+"F5.imprint","IMPRINT",FACE,{"disambiguationData":[TD([[makeQuery(id+"F5.imprint","IMPRINT",EDGE,{"disambiguationData":[TD([[subQ2,-1.0]])],"derivedFrom":subQ1}),-1.0]])]});}
            var Q11;
            {var subQ0=sQuery(id+"F5.wireOp",EDGE,"E35");var subQ1=sQuery(id+"F5.wireOp",EDGE,"E13");var subQ2=makeQuery(id+"F5.imprint","INTERSECT",VERTEX,{"disambiguationData":[OD(0.0)],"derivedFrom":[subQ1,subQ0]});Q11=makeQuery(id+"F5.imprint","IMPRINT",FACE,{"disambiguationData":[TD([[makeQuery(id+"F5.imprint","IMPRINT",EDGE,{"disambiguationData":[TD([[subQ2,-1.0]])],"derivedFrom":subQ1}),1.0]])]});}
            extrude(context, id + "F9", {"entities" : qUnion([Q0, Q1, Q2, Q3, Q4, Q5, Q6, Q7, Q8, Q9, Q10, Q11]), "operationType" : NewBodyOperationType.ADD, "depth" : 8 * mm, "offsetDistance" : 25 * mm});
        }
        {
            var Q0;
            Q0=makeQuery(id+"F9.opExtrude","CAP_EDGE",EDGE,{"disambiguationData":[OSD([sQuery(id+"F5.wireOp",EDGE,"E35")])],"isStart":false});
            var Q1;
            Q1=makeQuery(id+"F9.opExtrude","CAP_FACE",FACE,{"disambiguationData":[OSD([sQuery(id+"F5.wireOp",EDGE,"E31")])],"isStart":false});
            var Q2;
            Q2=makeQuery(id+"F9.opExtrude","CAP_FACE",FACE,{"disambiguationData":[OSD([sQuery(id+"F5.wireOp",EDGE,"E32")])],"isStart":false});
            var Q3;
            Q3=makeQuery(id+"F9.opExtrude","CAP_FACE",FACE,{"disambiguationData":[OSD([sQuery(id+"F5.wireOp",EDGE,"E33")])],"isStart":false});
            var Q4;
            Q4=makeQuery(id+"F9.opExtrude","CAP_FACE",FACE,{"disambiguationData":[OSD([sQuery(id+"F5.wireOp",EDGE,"E34")])],"isStart":false});
            var Q5;
            Q5=makeQuery(id+"F9.opExtrude","CAP_EDGE",EDGE,{"disambiguationData":[OSD([sQuery(id+"F5.wireOp",EDGE,"E36.left")])],"isStart":false});
            var Q6;
            Q6=makeQuery(id+"F9.opExtrude","CAP_EDGE",EDGE,{"disambiguationData":[OSD([sQuery(id+"F5.wireOp",EDGE,"E36.right")])],"isStart":false});
            var Q7;
            Q7=makeQuery(id+"F9.opExtrude","CAP_EDGE",EDGE,{"disambiguationData":[OSD([sQuery(id+"F5.wireOp",EDGE,"E36.bottom")])],"isStart":false});
            var Q8;
            Q8=makeQuery(id+"F9.opExtrude","CAP_EDGE",EDGE,{"disambiguationData":[OSD([sQuery(id+"F5.wireOp",EDGE,"E36.top")])],"isStart":false});
            fillet(context, id + "F10", {"entities" : qUnion([Q0, Q1, Q2, Q3, Q4, Q5, Q6, Q7, Q8]), "radius" : .45 * mm, "tangentPropagation" : true, "allowEdgeOverflow" : false});
        }
        {
            var Q0;
            {var subQ0=sQuery(id+"F5.wireOp",EDGE,"E35");var subQ1=sQuery(id+"F5.wireOp",EDGE,"E13");var subQ2=makeQuery(id+"F5.imprint","INTERSECT",VERTEX,{"disambiguationData":[OD(0.0)],"derivedFrom":[subQ1,subQ0]});Q0=makeQuery(id+"F5.imprint","IMPRINT",FACE,{"disambiguationData":[TD([[makeQuery(id+"F5.imprint","IMPRINT",EDGE,{"disambiguationData":[TD([[subQ2,-1.0]])],"derivedFrom":subQ1}),-1.0]])]});}
            var Q1;
            {var subQ0=sQuery(id+"F5.wireOp",EDGE,"E35");var subQ1=sQuery(id+"F5.wireOp",EDGE,"E13");var subQ2=makeQuery(id+"F5.imprint","INTERSECT",VERTEX,{"disambiguationData":[OD(0.0)],"derivedFrom":[subQ1,subQ0]});Q1=makeQuery(id+"F5.imprint","IMPRINT",FACE,{"disambiguationData":[TD([[makeQuery(id+"F5.imprint","IMPRINT",EDGE,{"disambiguationData":[TD([[subQ2,-1.0]])],"derivedFrom":subQ1}),1.0]])]});}
            var Q2;
            {var subQ1=sQuery(id+"F5.wireOp",EDGE,"E36.bottom");Q2=makeQuery(id+"F5.imprint","IMPRINT",FACE,{"disambiguationData":[TD([[makeQuery(id+"F5.imprint","IMPRINT",EDGE,{"derivedFrom":subQ1}),-1.0]])]});}
            var Q3;
            {var subQ0=sQuery(id+"F5.wireOp",EDGE,"E36.top");var subQ1=sQuery(id+"F5.wireOp",EDGE,"E13");var subQ2=makeQuery(id+"F5.imprint","INTERSECT",VERTEX,{"derivedFrom":[subQ1,subQ0]});Q3=makeQuery(id+"F5.imprint","IMPRINT",FACE,{"disambiguationData":[TD([[makeQuery(id+"F5.imprint","IMPRINT",EDGE,{"disambiguationData":[TD([[subQ2,-1.0]])],"derivedFrom":subQ1}),1.0]])]});}
            var Q4;
            {var subQ0=sQuery(id+"F5.wireOp",EDGE,"E34");var subQ1=sQuery(id+"F5.wireOp",EDGE,"E13");var subQ2=makeQuery(id+"F5.imprint","INTERSECT",VERTEX,{"disambiguationData":[OD(0.0)],"derivedFrom":[subQ1,subQ0]});Q4=makeQuery(id+"F5.imprint","IMPRINT",FACE,{"disambiguationData":[TD([[makeQuery(id+"F5.imprint","IMPRINT",EDGE,{"disambiguationData":[TD([[subQ2,-1.0]])],"derivedFrom":subQ1}),1.0]])]});}
            var Q5;
            {var subQ0=sQuery(id+"F5.wireOp",EDGE,"E34");var subQ1=sQuery(id+"F5.wireOp",EDGE,"E13");var subQ2=makeQuery(id+"F5.imprint","INTERSECT",VERTEX,{"disambiguationData":[OD(0.0)],"derivedFrom":[subQ1,subQ0]});Q5=makeQuery(id+"F5.imprint","IMPRINT",FACE,{"disambiguationData":[TD([[makeQuery(id+"F5.imprint","IMPRINT",EDGE,{"disambiguationData":[TD([[subQ2,-1.0]])],"derivedFrom":subQ1}),-1.0]])]});}
            var Q6;
            {var subQ0=sQuery(id+"F5.wireOp",EDGE,"E33");var subQ1=sQuery(id+"F5.wireOp",EDGE,"E13");var subQ2=makeQuery(id+"F5.imprint","INTERSECT",VERTEX,{"disambiguationData":[OD(0.0)],"derivedFrom":[subQ1,subQ0]});Q6=makeQuery(id+"F5.imprint","IMPRINT",FACE,{"disambiguationData":[TD([[makeQuery(id+"F5.imprint","IMPRINT",EDGE,{"disambiguationData":[TD([[subQ2,-1.0]])],"derivedFrom":subQ1}),1.0]])]});}
            var Q7;
            {var subQ0=sQuery(id+"F5.wireOp",EDGE,"E33");var subQ1=sQuery(id+"F5.wireOp",EDGE,"E13");var subQ2=makeQuery(id+"F5.imprint","INTERSECT",VERTEX,{"disambiguationData":[OD(0.0)],"derivedFrom":[subQ1,subQ0]});Q7=makeQuery(id+"F5.imprint","IMPRINT",FACE,{"disambiguationData":[TD([[makeQuery(id+"F5.imprint","IMPRINT",EDGE,{"disambiguationData":[TD([[subQ2,-1.0]])],"derivedFrom":subQ1}),-1.0]])]});}
            var Q8;
            {var subQ0=sQuery(id+"F5.wireOp",EDGE,"E32");var subQ1=sQuery(id+"F5.wireOp",EDGE,"E13");var subQ2=makeQuery(id+"F5.imprint","INTERSECT",VERTEX,{"disambiguationData":[OD(0.0)],"derivedFrom":[subQ1,subQ0]});Q8=makeQuery(id+"F5.imprint","IMPRINT",FACE,{"disambiguationData":[TD([[makeQuery(id+"F5.imprint","IMPRINT",EDGE,{"disambiguationData":[TD([[subQ2,-1.0]])],"derivedFrom":subQ1}),1.0]])]});}
            var Q9;
            {var subQ0=sQuery(id+"F5.wireOp",EDGE,"E32");var subQ1=sQuery(id+"F5.wireOp",EDGE,"E13");var subQ2=makeQuery(id+"F5.imprint","INTERSECT",VERTEX,{"disambiguationData":[OD(0.0)],"derivedFrom":[subQ1,subQ0]});Q9=makeQuery(id+"F5.imprint","IMPRINT",FACE,{"disambiguationData":[TD([[makeQuery(id+"F5.imprint","IMPRINT",EDGE,{"disambiguationData":[TD([[subQ2,-1.0]])],"derivedFrom":subQ1}),-1.0]])]});}
            var Q10;
            {var subQ0=sQuery(id+"F5.wireOp",EDGE,"E31");var subQ1=sQuery(id+"F5.wireOp",EDGE,"E13");var subQ2=makeQuery(id+"F5.imprint","INTERSECT",VERTEX,{"disambiguationData":[OD(0.0)],"derivedFrom":[subQ1,subQ0]});Q10=makeQuery(id+"F5.imprint","IMPRINT",FACE,{"disambiguationData":[TD([[makeQuery(id+"F5.imprint","IMPRINT",EDGE,{"disambiguationData":[TD([[subQ2,-1.0]])],"derivedFrom":subQ1}),-1.0]])]});}
            var Q11;
            {var subQ0=sQuery(id+"F5.wireOp",EDGE,"E31");var subQ1=sQuery(id+"F5.wireOp",EDGE,"E13");var subQ2=makeQuery(id+"F5.imprint","INTERSECT",VERTEX,{"disambiguationData":[OD(0.0)],"derivedFrom":[subQ1,subQ0]});Q11=makeQuery(id+"F5.imprint","IMPRINT",FACE,{"disambiguationData":[TD([[makeQuery(id+"F5.imprint","IMPRINT",EDGE,{"disambiguationData":[TD([[subQ2,-1.0]])],"derivedFrom":subQ1}),1.0]])]});}
            extrude(context, id + "F11", {"entities" : qUnion([Q0, Q1, Q2, Q3, Q4, Q5, Q6, Q7, Q8, Q9, Q10, Q11]), "operationType" : NewBodyOperationType.REMOVE, "depth" : 1.8 * mm, "offsetDistance" : 25 * mm});
        }
        {
            var Q0;
            Q0=qCreatedBy(makeId("Top.planeOp"),FACE);
            var sketch = newSketch(context, id + "F12", { "sketchPlane" : qUnion([Q0])});
            skCircle(sketch, "E37", {"center": v(0, 0) * mm, "radius": 13.47 * mm});
            skSolve(sketch);
        }
        {
            var Q0;
            Q0=makeQuery(id+"F12.imprint","IMPRINT",FACE,{"disambiguationData":[TD([[makeQuery(id+"F12.imprint","IMPRINT",EDGE,{"derivedFrom":sQuery(id+"F12.wireOp",EDGE,"E37")}),1.0]])]});
            extrude(context, id + "F13", {"entities" : qUnion([Q0]), "operationType" : NewBodyOperationType.REMOVE, "depth" : 1 * mm, "offsetDistance" : 25 * mm});
        }
        {
            var Q0;
            {var subQ0=sQuery(id+"F0.wireOp",EDGE,"E8.right");var subQ1=sQuery(id+"F0.wireOp",EDGE,"E1.0");var subQ2=makeQuery(id+"F0.imprint","INTERSECT",VERTEX,{"disambiguationData":[OD(1.0)],"derivedFrom":[subQ1,subQ0]});Q0=makeQuery(id+"F0.imprint","IMPRINT",FACE,{"disambiguationData":[TD([[makeQuery(id+"F0.imprint","IMPRINT",EDGE,{"disambiguationData":[TD([[subQ2,-1.0]])],"derivedFrom":subQ1}),1.0]])]});}
            var Q1;
            {var subQ0=sQuery(id+"F0.wireOp",EDGE,"E7.bottom");var subQ1=sQuery(id+"F0.wireOp",EDGE,"E1.0");var subQ2=makeQuery(id+"F0.imprint","INTERSECT",VERTEX,{"disambiguationData":[OD(1.0)],"derivedFrom":[subQ1,subQ0]});Q1=makeQuery(id+"F0.imprint","IMPRINT",FACE,{"disambiguationData":[TD([[makeQuery(id+"F0.imprint","IMPRINT",EDGE,{"disambiguationData":[TD([[subQ2,-1.0]])],"derivedFrom":subQ1}),1.0]])]});}
            var Q2;
            {var subQ0=sQuery(id+"F0.wireOp",EDGE,"E3.right");var subQ1=sQuery(id+"F0.wireOp",EDGE,"E1.0");var subQ2=makeQuery(id+"F0.imprint","INTERSECT",VERTEX,{"disambiguationData":[OD(0.0)],"derivedFrom":[subQ1,subQ0]});Q2=makeQuery(id+"F0.imprint","IMPRINT",FACE,{"disambiguationData":[TD([[makeQuery(id+"F0.imprint","IMPRINT",EDGE,{"disambiguationData":[TD([[subQ2,1.0]])],"derivedFrom":subQ1}),1.0]])]});}
            var Q3;
            {var subQ0=sQuery(id+"F0.wireOp",EDGE,"E2.left");var subQ1=sQuery(id+"F0.wireOp",EDGE,"E1.0");var subQ2=makeQuery(id+"F0.imprint","INTERSECT",VERTEX,{"disambiguationData":[OD(0.0)],"derivedFrom":[subQ1,subQ0]});Q3=makeQuery(id+"F0.imprint","IMPRINT",FACE,{"disambiguationData":[TD([[makeQuery(id+"F0.imprint","IMPRINT",EDGE,{"disambiguationData":[TD([[subQ2,-1.0]])],"derivedFrom":subQ1}),1.0]])]});}
            var Q4;
            {var subQ0=sQuery(id+"F0.wireOp",EDGE,"E9.left");var subQ1=sQuery(id+"F0.wireOp",EDGE,"E1.0");var subQ2=makeQuery(id+"F0.imprint","INTERSECT",VERTEX,{"disambiguationData":[OD(0.0)],"derivedFrom":[subQ1,subQ0]});Q4=makeQuery(id+"F0.imprint","IMPRINT",FACE,{"disambiguationData":[TD([[makeQuery(id+"F0.imprint","IMPRINT",EDGE,{"disambiguationData":[TD([[subQ2,-1.0]])],"derivedFrom":subQ1}),1.0]])]});}
            var Q5;
            {var subQ0=sQuery(id+"F0.wireOp",EDGE,"E7.top");var subQ1=sQuery(id+"F0.wireOp",EDGE,"E1.0");var subQ2=makeQuery(id+"F0.imprint","INTERSECT",VERTEX,{"disambiguationData":[OD(0.0)],"derivedFrom":[subQ1,subQ0]});Q5=makeQuery(id+"F0.imprint","IMPRINT",FACE,{"disambiguationData":[TD([[makeQuery(id+"F0.imprint","IMPRINT",EDGE,{"disambiguationData":[TD([[subQ2,-1.0]])],"derivedFrom":subQ1}),1.0]])]});}
            var Q6;
            {var subQ0=sQuery(id+"F0.wireOp",EDGE,"E6.top");var subQ1=sQuery(id+"F0.wireOp",EDGE,"E1.0");var subQ2=makeQuery(id+"F0.imprint","INTERSECT",VERTEX,{"disambiguationData":[OD(0.0)],"derivedFrom":[subQ1,subQ0]});Q6=makeQuery(id+"F0.imprint","IMPRINT",FACE,{"disambiguationData":[TD([[makeQuery(id+"F0.imprint","IMPRINT",EDGE,{"disambiguationData":[TD([[subQ2,-1.0]])],"derivedFrom":subQ1}),1.0]])]});}
            var Q7;
            {var subQ0=sQuery(id+"F0.wireOp",EDGE,"E3.right");var subQ1=sQuery(id+"F0.wireOp",EDGE,"E1.0");var subQ2=makeQuery(id+"F0.imprint","INTERSECT",VERTEX,{"disambiguationData":[OD(1.0)],"derivedFrom":[subQ1,subQ0]});Q7=makeQuery(id+"F0.imprint","IMPRINT",FACE,{"disambiguationData":[TD([[makeQuery(id+"F0.imprint","IMPRINT",EDGE,{"disambiguationData":[TD([[subQ2,-1.0]])],"derivedFrom":subQ1}),1.0]])]});}
            extrude(context, id + "F14", {"entities" : qUnion([Q0, Q1, Q2, Q3, Q4, Q5, Q6, Q7]), "operationType" : NewBodyOperationType.REMOVE, "depth" : 1 * mm, "offsetDistance" : 25 * mm});
        }
        {
            var Q0;
            Q0=makeQuery(id+"F14.boolean.opBoolean","COPY",EDGE,{"derivedFrom":makeQuery(id+"F14.opExtrude","SWEPT_EDGE",EDGE,{"disambiguationData":[OSD([sQuery(id+"F0.wireOp",EDGE,"E1.0"),sQuery(id+"F0.wireOp",EDGE,"E7.top")])]})});
            var Q1;
            {var subQ0=sQuery(id+"F0.wireOp",EDGE,"E6.top");var subQ1=sQuery(id+"F0.wireOp",EDGE,"E1.0");Q1=makeQuery(id+"F14.boolean.opBoolean","COPY",EDGE,{"derivedFrom":makeQuery(id+"F14.opExtrude","SWEPT_EDGE",EDGE,{"disambiguationData":[OSD([subQ1,subQ0]),TDD([makeQuery(id+"F0.imprint","INTERSECT",VERTEX,{"disambiguationData":[OD(0.0)],"derivedFrom":[subQ1,subQ0]})])]})});}
            var Q2;
            {var subQ0=sQuery(id+"F0.wireOp",EDGE,"E6.bottom");var subQ1=sQuery(id+"F0.wireOp",EDGE,"E1.0");Q2=makeQuery(id+"F14.boolean.opBoolean","COPY",EDGE,{"derivedFrom":makeQuery(id+"F14.opExtrude","SWEPT_EDGE",EDGE,{"disambiguationData":[OSD([subQ1,subQ0]),TDD([makeQuery(id+"F0.imprint","INTERSECT",VERTEX,{"disambiguationData":[OD(1.0)],"derivedFrom":[subQ1,subQ0]})])]})});}
            var Q3;
            {var subQ0=sQuery(id+"F0.wireOp",EDGE,"E7.bottom");var subQ1=sQuery(id+"F0.wireOp",EDGE,"E1.0");Q3=makeQuery(id+"F14.boolean.opBoolean","COPY",EDGE,{"derivedFrom":makeQuery(id+"F14.opExtrude","SWEPT_EDGE",EDGE,{"disambiguationData":[OSD([subQ1,subQ0]),TDD([makeQuery(id+"F0.imprint","INTERSECT",VERTEX,{"disambiguationData":[OD(0.0)],"derivedFrom":[subQ1,subQ0]})])]})});}
            var Q4;
            Q4=makeQuery(id+"F14.boolean.opBoolean","COPY",EDGE,{"derivedFrom":makeQuery(id+"F14.opExtrude","SWEPT_EDGE",EDGE,{"disambiguationData":[OSD([sQuery(id+"F0.wireOp",EDGE,"E1.0"),sQuery(id+"F0.wireOp",EDGE,"E3.left")])]})});
            var Q5;
            {var subQ0=sQuery(id+"F0.wireOp",EDGE,"E2.left");var subQ1=sQuery(id+"F0.wireOp",EDGE,"E1.0");Q5=makeQuery(id+"F14.boolean.opBoolean","COPY",EDGE,{"derivedFrom":makeQuery(id+"F14.opExtrude","SWEPT_EDGE",EDGE,{"disambiguationData":[OSD([subQ1,subQ0]),TDD([makeQuery(id+"F0.imprint","INTERSECT",VERTEX,{"disambiguationData":[OD(1.0)],"derivedFrom":[subQ1,subQ0]})])]})});}
            var Q6;
            {var subQ0=sQuery(id+"F0.wireOp",EDGE,"E3.right");var subQ1=sQuery(id+"F0.wireOp",EDGE,"E1.0");Q6=makeQuery(id+"F14.boolean.opBoolean","COPY",EDGE,{"derivedFrom":makeQuery(id+"F14.opExtrude","SWEPT_EDGE",EDGE,{"disambiguationData":[OSD([subQ1,subQ0]),TDD([makeQuery(id+"F0.imprint","INTERSECT",VERTEX,{"disambiguationData":[OD(1.0)],"derivedFrom":[subQ1,subQ0]})])]})});}
            var Q7;
            {var subQ0=sQuery(id+"F0.wireOp",EDGE,"E9.left");var subQ1=sQuery(id+"F0.wireOp",EDGE,"E1.0");Q7=makeQuery(id+"F14.boolean.opBoolean","COPY",EDGE,{"derivedFrom":makeQuery(id+"F14.opExtrude","SWEPT_EDGE",EDGE,{"disambiguationData":[OSD([subQ1,subQ0]),TDD([makeQuery(id+"F0.imprint","INTERSECT",VERTEX,{"disambiguationData":[OD(0.0)],"derivedFrom":[subQ1,subQ0]})])]})});}
            var Q8;
            {var subQ0=sQuery(id+"F0.wireOp",EDGE,"E8.right");var subQ1=sQuery(id+"F0.wireOp",EDGE,"E1.0");Q8=makeQuery(id+"F14.boolean.opBoolean","COPY",EDGE,{"derivedFrom":makeQuery(id+"F14.opExtrude","SWEPT_EDGE",EDGE,{"disambiguationData":[OSD([subQ1,subQ0]),TDD([makeQuery(id+"F0.imprint","INTERSECT",VERTEX,{"disambiguationData":[OD(0.0)],"derivedFrom":[subQ1,subQ0]})])]})});}
            var Q9;
            {var subQ0=sQuery(id+"F0.wireOp",EDGE,"E8.right");var subQ1=sQuery(id+"F0.wireOp",EDGE,"E1.0");Q9=makeQuery(id+"F14.boolean.opBoolean","COPY",EDGE,{"derivedFrom":makeQuery(id+"F14.opExtrude","SWEPT_EDGE",EDGE,{"disambiguationData":[OSD([subQ1,subQ0]),TDD([makeQuery(id+"F0.imprint","INTERSECT",VERTEX,{"disambiguationData":[OD(1.0)],"derivedFrom":[subQ1,subQ0]})])]})});}
            var Q10;
            {var subQ0=sQuery(id+"F0.wireOp",EDGE,"E9.left");var subQ1=sQuery(id+"F0.wireOp",EDGE,"E1.0");Q10=makeQuery(id+"F14.boolean.opBoolean","COPY",EDGE,{"derivedFrom":makeQuery(id+"F14.opExtrude","SWEPT_EDGE",EDGE,{"disambiguationData":[OSD([subQ1,subQ0]),TDD([makeQuery(id+"F0.imprint","INTERSECT",VERTEX,{"disambiguationData":[OD(1.0)],"derivedFrom":[subQ1,subQ0]})])]})});}
            var Q11;
            {var subQ0=sQuery(id+"F0.wireOp",EDGE,"E7.bottom");var subQ1=sQuery(id+"F0.wireOp",EDGE,"E1.0");Q11=makeQuery(id+"F14.boolean.opBoolean","COPY",EDGE,{"derivedFrom":makeQuery(id+"F14.opExtrude","SWEPT_EDGE",EDGE,{"disambiguationData":[OSD([subQ1,subQ0]),TDD([makeQuery(id+"F0.imprint","INTERSECT",VERTEX,{"disambiguationData":[OD(1.0)],"derivedFrom":[subQ1,subQ0]})])]})});}
            var Q12;
            {var subQ0=sQuery(id+"F0.wireOp",EDGE,"E6.bottom");var subQ1=sQuery(id+"F0.wireOp",EDGE,"E1.0");Q12=makeQuery(id+"F14.boolean.opBoolean","COPY",EDGE,{"derivedFrom":makeQuery(id+"F14.opExtrude","SWEPT_EDGE",EDGE,{"disambiguationData":[OSD([subQ1,subQ0]),TDD([makeQuery(id+"F0.imprint","INTERSECT",VERTEX,{"disambiguationData":[OD(0.0)],"derivedFrom":[subQ1,subQ0]})])]})});}
            var Q13;
            {var subQ0=sQuery(id+"F0.wireOp",EDGE,"E2.left");var subQ1=sQuery(id+"F0.wireOp",EDGE,"E1.0");Q13=makeQuery(id+"F14.boolean.opBoolean","COPY",EDGE,{"derivedFrom":makeQuery(id+"F14.opExtrude","SWEPT_EDGE",EDGE,{"disambiguationData":[OSD([subQ1,subQ0]),TDD([makeQuery(id+"F0.imprint","INTERSECT",VERTEX,{"disambiguationData":[OD(0.0)],"derivedFrom":[subQ1,subQ0]})])]})});}
            var Q14;
            {var subQ0=sQuery(id+"F0.wireOp",EDGE,"E3.right");var subQ1=sQuery(id+"F0.wireOp",EDGE,"E1.0");Q14=makeQuery(id+"F14.boolean.opBoolean","COPY",EDGE,{"derivedFrom":makeQuery(id+"F14.opExtrude","SWEPT_EDGE",EDGE,{"disambiguationData":[OSD([subQ1,subQ0]),TDD([makeQuery(id+"F0.imprint","INTERSECT",VERTEX,{"disambiguationData":[OD(0.0)],"derivedFrom":[subQ1,subQ0]})])]})});}
            var Q15;
            {var subQ0=sQuery(id+"F0.wireOp",EDGE,"E6.top");var subQ1=sQuery(id+"F0.wireOp",EDGE,"E1.0");Q15=makeQuery(id+"F14.boolean.opBoolean","COPY",EDGE,{"derivedFrom":makeQuery(id+"F14.opExtrude","SWEPT_EDGE",EDGE,{"disambiguationData":[OSD([subQ1,subQ0]),TDD([makeQuery(id+"F0.imprint","INTERSECT",VERTEX,{"disambiguationData":[OD(1.0)],"derivedFrom":[subQ1,subQ0]})])]})});}
            fillet(context, id + "F15", {"entities" : qUnion([Q0, Q1, Q2, Q3, Q4, Q5, Q6, Q7, Q8, Q9, Q10, Q11, Q12, Q13, Q14, Q15]), "radius" : 1 * mm, "tangentPropagation" : true, "allowEdgeOverflow" : false});
        }
    });
